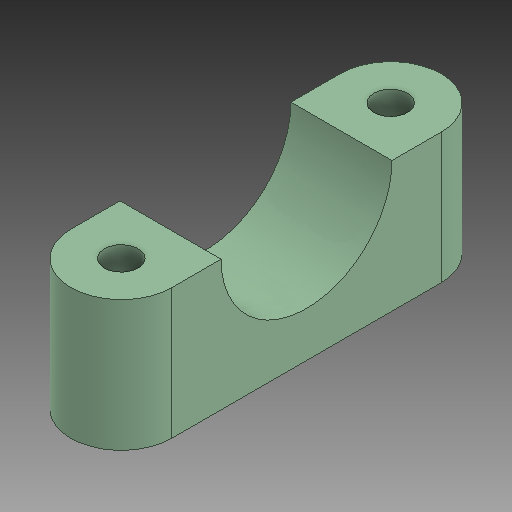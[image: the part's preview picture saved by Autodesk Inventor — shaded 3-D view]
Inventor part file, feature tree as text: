
AUTODESK INVENTOR PART (.ipt)
format: ipt  version: 2020 (Build 240168000, 168)  size: 152,064 bytes
history: native  units: mm
features: extrude x3, sketch x3, other x1
ambient origin geometry x8: Origin, YZ Plane, XZ Plane, XY Plane, X Axis, Y Axis, Z Axis, Center Point
bodies: Body1 (feature_tree)
feature tree (7):
  other  "Твердое тело1"
  extrude  "Выдавливание1"  Depth=15.0mm
  extrude  "Выдавливание2"  Depth=44.0mm
  extrude  "Выдавливание3"  Depth=16.0mm
  sketch  "Эскиз1"
  sketch  "Эскиз2"
  sketch  "Эскиз4"
